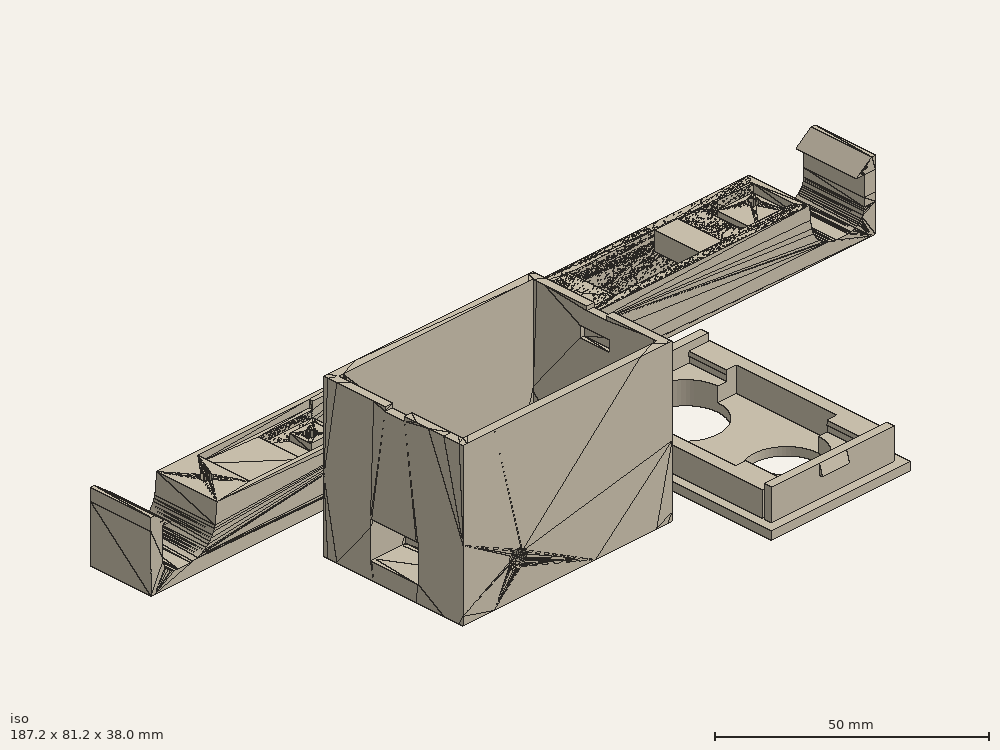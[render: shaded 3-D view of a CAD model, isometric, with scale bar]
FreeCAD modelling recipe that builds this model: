
FCSTD DOCUMENT  (FreeCAD 0.19R)
Label: station.sensor.V2
License: All rights reserved
LicenseURL: http://en.wikipedia.org/wiki/All_rights_reserved
objects: Part::Extrusion×16, Part::Cut×12, Part::Feature×11, Part::Part2DObjectPython×11, Part::MultiFuse×4
note: 54 computed .brp shape members not serialized (recipe doc carries the construction recipe); baked Part::Feature solids carry a one-line shape summary decoded from their .brp

FEATURE [Part::Feature] Fusion005002002014004003003002009002010004002003006003008008004007002004008002005003003004013003004015003002008009002007002001001  label="Unnamed001"
FEATURE [Part::Feature] Cut002001  label="Cut004008021006004001003007014046"
  shape: bbox 54 x 35.95 x 38 mm, 98 faces (baked)
FEATURE [Part::Feature] Fusion005002002014004003003002009002010004002003006003008008004007002004008002005003003004013003004015003002008009002005002002005002  label="Fusion005002002014004003003002009002010004002003006003008008004007002004008002005003003004013003004015003002008009002007004"
  shape: bbox 35.95 x 54 x 9.5 mm, 61 faces (baked)
FEATURE [Part::Feature] Fusion005002002014004003003002009002010004002003006003008008004007002004008002005003003004013003004015003002008009002005002002005001  label="Fusion005002002014004003003002009002010004002003006003008008004007002004008002005003003004013003004015003002008009002005002002045"
  shape: bbox 187.2 x 15.6 x 16.67 mm, 79 faces (baked)
FEATURE [Part::Extrusion] Extrusion001
  Dir = (1.02063e-10,-1.9625,-8.10301e-10)
  DirMode = 0
  FaceMakerClass = Part::FaceMakerBullseye
  LengthFwd = 0
  LengthRev = 0
  Placement = pos=(76.3793,63.9738,-45.9478) rot=(-0.57735,0.57735,0.57735;4.18879rad)
  Solid = true
  Symmetric = false
FEATURE [Part::Extrusion] Extrusion
  Dir = (-2.77136e-09,53.2889,2.20027e-08)
  DirMode = 0
  FaceMakerClass = Part::FaceMakerBullseye
  LengthFwd = 0
  LengthRev = 0
  Placement = pos=(76.3793,63.9738,-72.5923) rot=(-0.57735,0.57735,0.57735;4.18879rad)
  Solid = true
  Symmetric = false
FEATURE [Part::Part2DObjectPython] Rectangle  # Draft 2D object (typed FeaturePython)
  ChamferSize = 0
  Columns = 1
  FilletRadius = 0
  Height = 11.4608
  Length = 24.7945
  MakeFace = true
  Placement = pos=(242.085,-118.422,-178.501) rot=(0,0,1;0rad)
  Rows = 1
FEATURE [Part::Extrusion] Extrusion002
  Base = -> Rectangle
  Dir = (8.1e-15,-2.78e-14,-4.5)
  DirMode = 0
  FaceMakerClass = Part::FaceMakerBullseye
  LengthFwd = 0
  LengthRev = 0
  Solid = true
  Symmetric = false
FEATURE [Part::Cut] Cut
  Base = -> Extrusion002
  Tool = -> Extrusion001
FEATURE [Part::Cut] Cut002002
  Base = -> Cut
  Tool = -> Extrusion
FEATURE [Part::Part2DObjectPython] Rectangle001  # Draft 2D object (typed FeaturePython)
  ChamferSize = 0
  Columns = 1
  FilletRadius = 0
  Height = 10.5
  Length = 4
  MakeFace = true
  Placement = pos=(253.58,-118.012,-178.501) rot=(0,0,1;0rad)
  Rows = 1
FEATURE [Part::Extrusion] Extrusion003
  Base = -> Rectangle001
  Dir = (9.12e-14,-3.108e-13,-50.3674)
  DirMode = 0
  FaceMakerClass = Part::FaceMakerBullseye
  LengthFwd = 0
  LengthRev = 0
  Solid = true
  Symmetric = false
FEATURE [Part::Cut] Cut002003
  Base = -> Cut002002
  Tool = -> Extrusion003
FEATURE [Part::Part2DObjectPython] Rectangle002  # Draft 2D object (typed FeaturePython)
  ChamferSize = 0
  Columns = 1
  FilletRadius = 0
  Height = 11.6
  Length = 56.8721
  MakeFace = true
  Placement = pos=(210.008,-106.962,-191.501) rot=(1,0,0;3.14159rad)
  Rows = 1
  Support = -> [Fusion005002002014004003003002009002010004002003006003008008004007002004008002005003003004013003004015003002008009002005002002005001]
FEATURE [Part::Extrusion] Extrusion004
  Base = -> Rectangle002
  Dir = (2e-15,3.635e-13,1)
  DirMode = 0
  FaceMakerClass = Part::FaceMakerBullseye
  LengthFwd = 0
  LengthRev = 0
  Solid = true
  Symmetric = false
FEATURE [Part::MultiFuse] Fusion
  Shapes = -> [Fusion005002002014004003003002009002010004002003006003008008004007002004008002005003003004013003004015003002008009002005002002005001,Extrusion004]
FEATURE [Part::MultiFuse] Fusion005002002014004003003002009002010004002003006003008008004007002004008002005003003004013003004015003002008009002005002002005003
  Shapes = -> [Fusion,Cut002003]
FEATURE [Part::Feature] Fusion005002002014004003003002009002010004002003006003008008004007002004008002005003003004013003004015003002008009002005002002005003001  label="Fusion005002002014004003003002009002010004002003006003008008004007002004008002005003003004013003004015003002008009002005002002005004"
  shape: bbox 187.2 x 15.6 x 16.67 mm, 91 faces (baked)
FEATURE [Part::Part2DObjectPython] Rectangle003  # Draft 2D object (typed FeaturePython)
  ChamferSize = 0
  Columns = 1
  FilletRadius = 0
  Height = 2.5
  Length = 11.6
  MakeFace = true
  Placement = pos=(242.085,-106.962,-183.001) rot=(0.57735,-0.57735,-0.57735;2.0944rad)
  Rows = 1
  Support = -> [Fusion005002002014004003003002009002010004002003006003008008004007002004008002005003003004013003004015003002008009002005002002005003001]
FEATURE [Part::Extrusion] Extrusion005
  Base = -> Rectangle003
  Dir = (11.4945,6.4e-15,-7e-15)
  DirMode = 0
  FaceMakerClass = Part::FaceMakerBullseye
  LengthFwd = 0
  LengthRev = 0
  Solid = true
  Symmetric = false
FEATURE [Part::Cut] Cut002004
  Base = -> Fusion005002002014004003003002009002010004002003006003008008004007002004008002005003003004013003004015003002008009002005002002005003001
  Tool = -> Extrusion005
FEATURE [Part::Feature] Face
  shape: bbox 24.8 x 0.000473 x 4.5 mm, 1 faces, 0 solids (baked)
FEATURE [Part::Extrusion] Extrusion006
  Base = -> Face
  Dir = (0,-0.139156,9e-16)
  DirMode = 0
  FaceMakerClass = Part::FaceMakerBullseye
  LengthFwd = 0
  LengthRev = 0
  Solid = true
  Symmetric = false
FEATURE [Part::MultiFuse] Fusion005002002014004003003002009002010004002003006003008008004007002004008002005003003004013003004015003002008009002005002002005003002
  Shapes = -> [Extrusion006,Cut002004]
FEATURE [Part::Feature] Fusion005002002014004003003002009002010004002003006003008008004007002004008002005003003004013003004015003002008009002005002002005003002001  label="Fusion005002002014004003003002009002010004002003006003008008004007002004008002005003003004013003004015003002008009002005002002005003003"
  shape: bbox 187.2 x 15.6 x 16.67 mm, 93 faces (baked)
FEATURE [Part::Part2DObjectPython] Rectangle004  # Draft 2D object (typed FeaturePython)
  ChamferSize = 0
  Columns = 1
  FilletRadius = 0
  Height = 11.6
  Length = 6
  MakeFace = true
  Placement = pos=(242.085,-118.562,-178.501) rot=(0,0,1;0rad)
  Rows = 1
FEATURE [Part::Extrusion] Extrusion007
  Base = -> Rectangle004
  Dir = (3e-15,-1.93e-14,-2)
  DirMode = 0
  FaceMakerClass = Part::FaceMakerBullseye
  LengthFwd = 0
  LengthRev = 0
  Solid = true
  Symmetric = false
FEATURE [Part::Cut] Cut002005
  Base = -> Fusion005002002014004003003002009002010004002003006003008008004007002004008002005003003004013003004015003002008009002005002002005003002001
  Tool = -> Extrusion007
FEATURE [Part::Part2DObjectPython] Rectangle005  # Draft 2D object (typed FeaturePython)
  ChamferSize = 0
  Columns = 1
  FilletRadius = 0
  Height = 11.6
  Length = 10
  MakeFace = true
  Placement = pos=(210.008,-118.562,-178.501) rot=(0,0,1;0rad)
  Rows = 1
FEATURE [Part::Extrusion] Extrusion008
  Base = -> Rectangle005
  Dir = (4.5e-15,-8.7e-15,-2)
  DirMode = 0
  FaceMakerClass = Part::FaceMakerBullseye
  LengthFwd = 0
  LengthRev = 0
  Solid = true
  Symmetric = false
FEATURE [Part::MultiFuse] Fusion005002002014004003003002009002010004002003006003008008004007002004008002005003003004013003004015003002008009002005002002005003002002
  Shapes = -> [Extrusion008,Cut002005]
FEATURE [Part::Feature] Fusion005002002014004003003002009002010004002003006003008008004007002004008002005003003004013003004015003002008009002005002002005003002002001  label="Fusion005002002014004003003002009002010004002003006003008008004007002004008002005003003004013003004015003002008009002005002002005003002003"
  shape: bbox 187.2 x 15.6 x 16.67 mm, 94 faces (baked)
FEATURE [Part::Feature] Face001
  shape: bbox 11 x 0.0002686 x 11.5 mm, 1 faces, 0 solids (baked)
FEATURE [Part::Extrusion] Extrusion009
  Base = -> Face001
  Dir = (0,-0.15,-1.09518e-11)
  DirMode = 0
  FaceMakerClass = Part::FaceMakerBullseye
  LengthFwd = 0
  LengthRev = 0
  Solid = true
  Symmetric = false
FEATURE [Part::Cut] Cut002006
  Base = -> Cut002001
  Tool = -> Extrusion009
FEATURE [Part::Feature] Face002
  shape: bbox 5.8 x 9.455e-05 x 5.8 mm, 1 faces, 0 solids (baked)
FEATURE [Part::Extrusion] Extrusion010
  Base = -> Face002
  Dir = (1.7859e-11,-1,1.46555e-10)
  DirMode = 0
  FaceMakerClass = Part::FaceMakerBullseye
  LengthFwd = 0
  LengthRev = 0
  Solid = true
  Symmetric = false
FEATURE [Part::Cut] Cut002007
  Base = -> Cut002006
  Tool = -> Extrusion010
FEATURE [Part::Part2DObjectPython] Circle  # Draft 2D object (typed FeaturePython)
  FirstAngle = 0
  LastAngle = 0
  MakeFace = true
  Placement = pos=(168.62,-144.553,-190.001) rot=(0,0,1;0rad)
  Radius = 1.51
FEATURE [Part::Extrusion] Extrusion011
  Base = -> Circle
  Dir = (5.1056e-09,-1.98264e-09,27.155)
  DirMode = 0
  FaceMakerClass = Part::FaceMakerBullseye
  LengthFwd = 0
  LengthRev = 0
  Solid = true
  Symmetric = false
FEATURE [Part::Cut] Cut002008
  Base = -> Cut002007
  Tool = -> Extrusion011
FEATURE [Part::Feature] Cut002008001  label="Cut004008021006004001003007014047"
  shape: bbox 54 x 35.95 x 38 mm, 89 faces (baked)
FEATURE [Part::Part2DObjectPython] Rectangle006  # Draft 2D object (typed FeaturePython)
  Area = 34.8
  ChamferSize = 0
  Columns = 1
  FilletRadius = 0
  Height = 11.6
  Length = 3
  MakeFace = true
  Placement = pos=(150.736,-118.562,-182.001) rot=(0,0,1;0rad)
  Rows = 1
FEATURE [Part::Extrusion] Extrusion012
  Base = -> Rectangle006
  Dir = (2e-16,-3.635e-13,-1)
  DirMode = 0
  FaceMakerClass = Part::FaceMakerBullseye
  LengthFwd = 0
  LengthRev = 0
  Solid = true
  Symmetric = false
FEATURE [Part::Cut] Cut002008002
  Base = -> Fusion005002002014004003003002009002010004002003006003008008004007002004008002005003003004013003004015003002008009002005002002005003002002001
  Tool = -> Extrusion012
FEATURE [Part::Part2DObjectPython] Wire  # Draft 2D object (typed FeaturePython)
  Area = 34.0899
  ChamferSize = 0
  Closed = true
  End = (273.725,-120.562,-181.946)
  FilletRadius = 0
  Length = 27.1889
  MakeFace = true
  Placement = pos=(282.506,-120.562,-177.83) rot=(1,0,0;1.5708rad)
  Points = (3) [(0,0,0),(-9.42291,3.34794,1.98952e-13),(-8.78126,-4.11557,-2.84217e-13)]
  Start = (282.506,-120.562,-177.83)
  Subdivisions = 0
FEATURE [Part::Extrusion] Extrusion013
  Base = -> Wire
  Dir = (1.42e-14,58.3008,1.0744e-12)
  DirMode = 0
  FaceMakerClass = Part::FaceMakerBullseye
  LengthFwd = 0
  LengthRev = 0
  Solid = true
  Symmetric = false
FEATURE [Part::Cut] Cut002008003
  Base = -> Cut002008002
  Tool = -> Extrusion013
FEATURE [Part::Part2DObjectPython] Wire001  # Draft 2D object (typed FeaturePython)
  Area = 42.989
  ChamferSize = 0
  Closed = true
  End = (110.9,-120.562,-182.026)
  FilletRadius = 0
  Length = 30.8639
  MakeFace = true
  Placement = pos=(101.29,-120.562,-177.837) rot=(1,0,0;1.5708rad)
  Points = (3) [(0,0,0),(11.3075,4.01753,1.27898e-13),(9.61005,-4.18919,4.54747e-13)]
  Start = (101.29,-120.562,-177.837)
  Subdivisions = 0
FEATURE [Part::Extrusion] Extrusion014
  Base = -> Wire001
  Dir = (9.315e-13,38.2052,-3.6645e-12)
  DirMode = 0
  FaceMakerClass = Part::FaceMakerBullseye
  LengthFwd = 0
  LengthRev = 0
  Solid = true
  Symmetric = false
FEATURE [Part::Cut] Cut002008004
  Base = -> Cut002008003
  Tool = -> Extrusion014
FEATURE [Part::Part2DObjectPython] Rectangle007  # Draft 2D object (typed FeaturePython)
  Area = 11.6
  ChamferSize = 0
  Columns = 1
  FilletRadius = 0
  Height = 1
  Length = 11.6
  MakeFace = true
  Placement = pos=(248.085,-118.562,-179.501) rot=(0.57735,0.57735,-0.57735;4.18879rad)
  Rows = 1
FEATURE [Part::Extrusion] Extrusion015
  Base = -> Rectangle007
  Dir = (5.49454,7.3e-15,-7.3e-15)
  DirMode = 0
  FaceMakerClass = Part::FaceMakerBullseye
  LengthFwd = 0
  LengthRev = 0
  Solid = true
  Symmetric = false
FEATURE [Part::Cut] Cut002008005
  Base = -> Cut002008004
  Tool = -> Extrusion015
